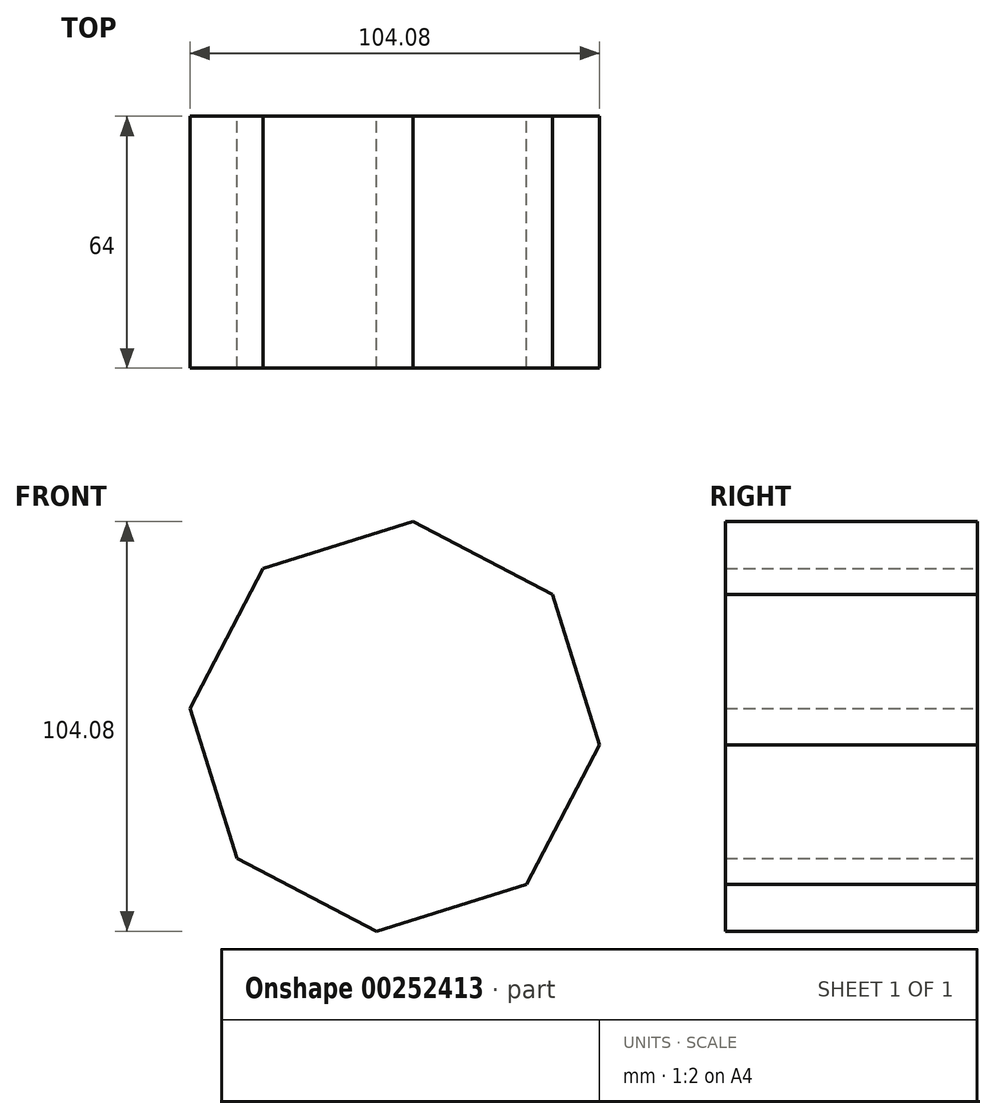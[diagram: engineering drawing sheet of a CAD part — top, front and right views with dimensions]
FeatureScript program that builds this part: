
annotation { "Feature Type Name" : "Feature", "Feature Type Description" : "" }
export const myFeature = defineFeature(function(context is Context, id is Id, definition is map)
    precondition{}
    {
        {
            var Q0;
            Q0=qCreatedBy(makeId("Front.planeOp"),FACE);
            var sketch = newSketch(context, id + "F0", { "sketchPlane" : qUnion([Q0])});
            skCircle(sketch, "E0.cCircle", {"center": v(0, 0) * mm, "radius": 52.25 * mm, "construction": true});
            skLineSegment(sketch, "E0.0", {"start": v(-33.52, 40.08) * mm, "end": v(4.64, 52.04) * mm});
            skLineSegment(sketch, "E0.1", {"start": v(4.64, 52.04) * mm, "end": v(40.08, 33.52) * mm});
            skLineSegment(sketch, "E0.2", {"start": v(40.08, 33.52) * mm, "end": v(52.04, -4.64) * mm});
            skLineSegment(sketch, "E0.3", {"start": v(52.04, -4.64) * mm, "end": v(33.52, -40.08) * mm});
            skLineSegment(sketch, "E0.4", {"start": v(33.52, -40.08) * mm, "end": v(-4.64, -52.04) * mm});
            skLineSegment(sketch, "E0.5", {"start": v(-4.64, -52.04) * mm, "end": v(-40.08, -33.52) * mm});
            skLineSegment(sketch, "E0.6", {"start": v(-40.08, -33.52) * mm, "end": v(-52.04, 4.64) * mm});
            skLineSegment(sketch, "E0.7", {"start": v(-52.04, 4.64) * mm, "end": v(-33.52, 40.08) * mm});
            skSolve(sketch);
        }
        {
            var Q0;
            Q0 = qSketchRegion(id + "F0", true);
            extrude(context, id + "F1", {"entities" : qUnion([Q0]), "endBound" : BoundingType.SYMMETRIC, "depth" : 64 * mm});
        }
    });
